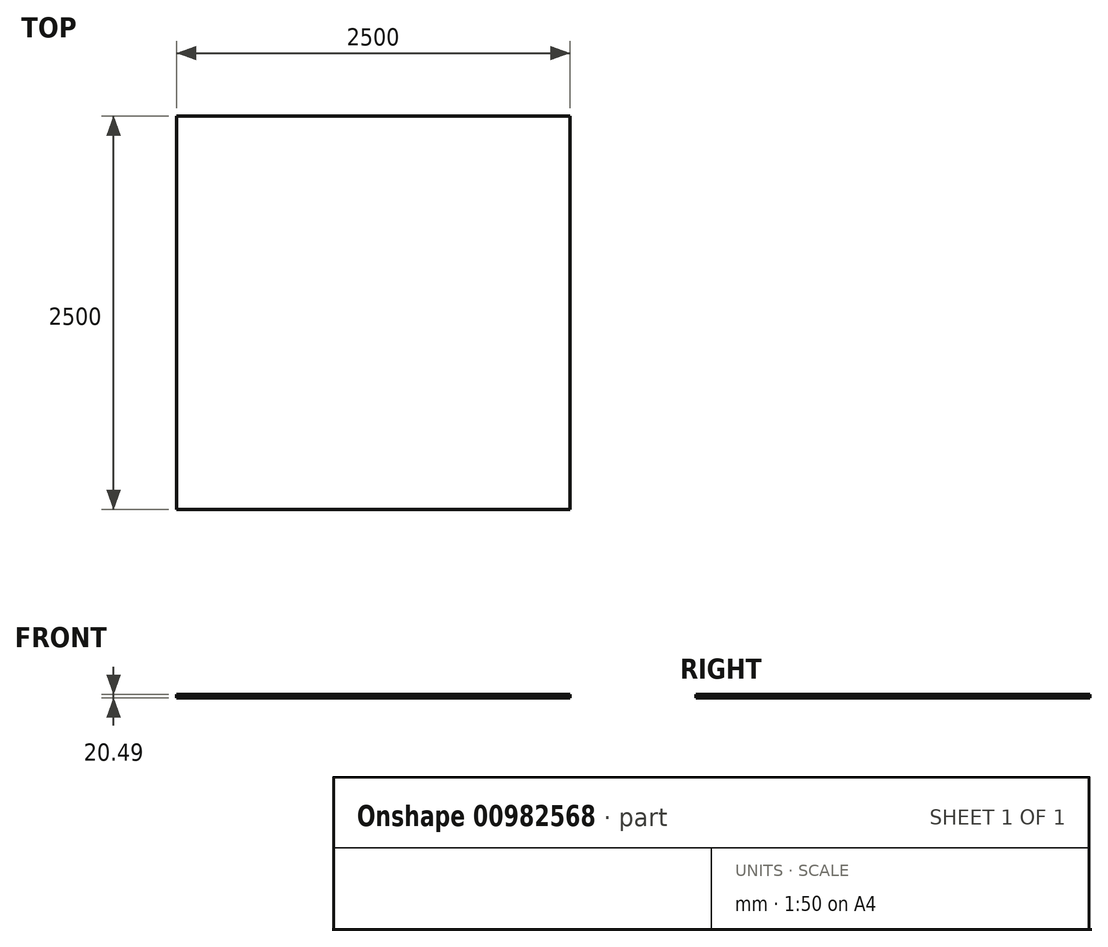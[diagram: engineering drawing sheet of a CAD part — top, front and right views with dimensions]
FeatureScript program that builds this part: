
annotation { "Feature Type Name" : "Feature", "Feature Type Description" : "" }
export const myFeature = defineFeature(function(context is Context, id is Id, definition is map)
    precondition{}
    {
        {
            var Q0;
            Q0=qCreatedBy(makeId("Top.planeOp"),FACE);
            var sketch = newSketch(context, id + "F0", { "sketchPlane" : qUnion([Q0])});
            skLineSegment(sketch, "E0.bottom", {"start": v(-1250, -1250) * mm, "end": v(1250, -1250) * mm});
            skLineSegment(sketch, "E0.top", {"start": v(-1250, 1250) * mm, "end": v(1250, 1250) * mm});
            skLineSegment(sketch, "E0.left", {"start": v(-1250, -1250) * mm, "end": v(-1250, 1250) * mm});
            skLineSegment(sketch, "E0.right", {"start": v(1250, -1250) * mm, "end": v(1250, 1250) * mm});
            skSolve(sketch);
        }
        {
            var Q0;
            Q0=qCreatedBy(makeId("Front.planeOp"),FACE);
            var sketch = newSketch(context, id + "F1", { "sketchPlane" : qUnion([Q0])});
            skLineSegment(sketch, "E1", {"start": v(0, 0) * mm, "end": v(0, 20.5) * mm});
            skSolve(sketch);
        }
        {
            var Q0;
            Q0=makeQuery(id+"F0.imprint","IMPRINT",FACE,{"disambiguationData":[TD([[makeQuery(id+"F0.imprint","IMPRINT",EDGE,{"derivedFrom":sQuery(id+"F0.wireOp",EDGE,"E0.bottom")}),1.0]])]});
            var Q1;
            Q1=sQuery(id+"F1.wireOp",EDGE,"E1");
            sweep(context, id + "F2", {"profiles" : qUnion([Q0]), "path" : qUnion([Q1])});
        }
    });
